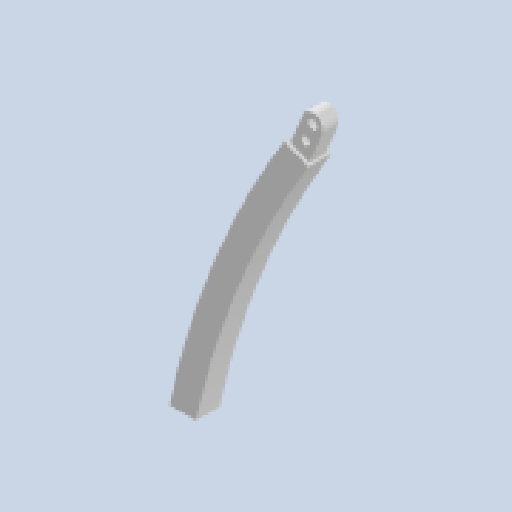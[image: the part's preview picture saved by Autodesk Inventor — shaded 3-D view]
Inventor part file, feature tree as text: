
AUTODESK INVENTOR PART (.ipt)
format: ipt  version: 2025.2 (Build 292293000, 293)  size: 112,128 bytes
history: native  units: mm
features: extrude x2, sketch x1
ambient origin geometry x8: Origin, YZ Plane, XZ Plane, XY Plane, X Axis, Y Axis, Z Axis, Center Point
bodies: Solid1 (feature_tree)
feature tree (3):
  sketch  "Sketch1"  dims[d4=3.0mm d5=294.5mm d7=3.0mm d8=6.5mm d9=3.5mm d10=300.0mm d11=1.0mm d12=1.0mm d13=100.0mm d14=5.5mm d15=0.0mm d16=8.0mm d17=0.0mm d18=289.75mm]
  extrude  "Extrusion1"  Depth=3.5mm
  extrude  "Extrusion2"  Depth=300.0mm
